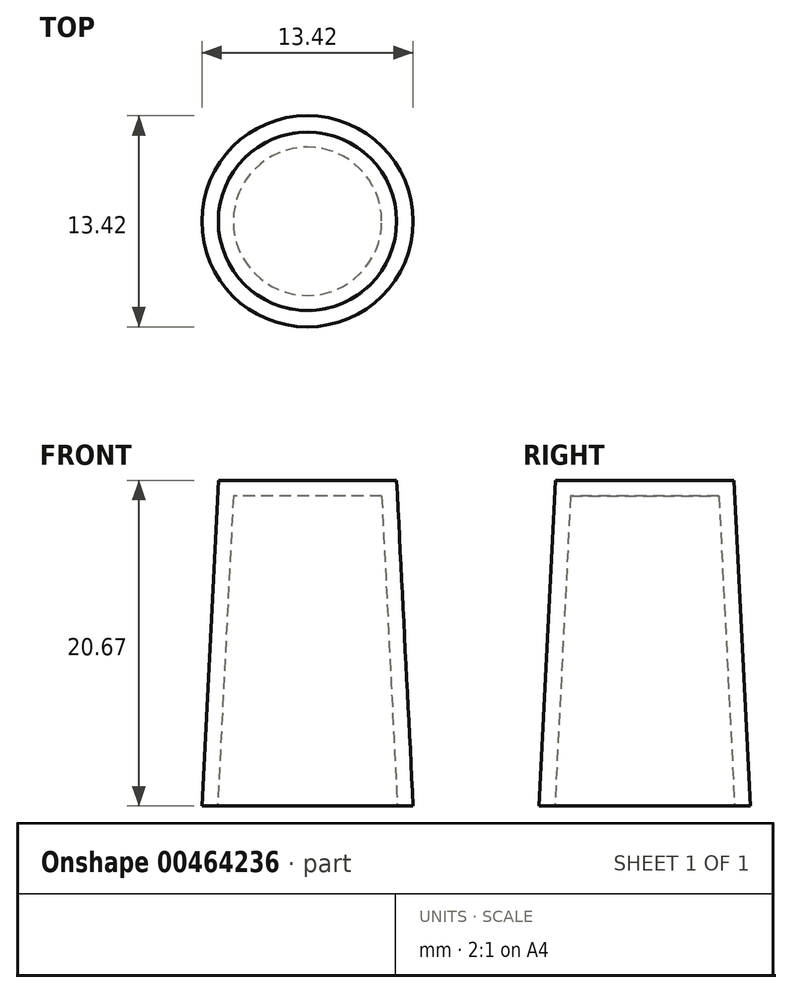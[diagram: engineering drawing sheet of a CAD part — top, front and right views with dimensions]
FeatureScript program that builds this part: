
annotation { "Feature Type Name" : "Feature", "Feature Type Description" : "" }
export const myFeature = defineFeature(function(context is Context, id is Id, definition is map)
    precondition{}
    {
        {
            var Q0;
            Q0=qCreatedBy(makeId("Top.planeOp"),FACE);
            var sketch = newSketch(context, id + "F0", { "sketchPlane" : qUnion([Q0])});
            skCircle(sketch, "E0", {"center": v(0, 0) * mm, "radius": 6.71 * mm});
            skSolve(sketch);
        }
        {
            var Q0;
            Q0 = qSketchRegion(id + "F0", true);
            extrude(context, id + "F1", {"entities" : qUnion([Q0]), "depth" : 20.67 * mm, "hasDraft" : true, "draftAngle" : 2.9 * degree, "draftPullDirection" : true});
        }
        {
            var Q0;
            Q0=makeQuery(id+"F1.opExtrude","CAP_FACE",FACE,{"disambiguationData":[OSD([sQuery(id+"F0.wireOp",EDGE,"E0")])],"isStart":true});
            shell(context, id + "F2", {"entities" : qUnion([Q0]), "thickness" : 1 * mm});
        }
    });
